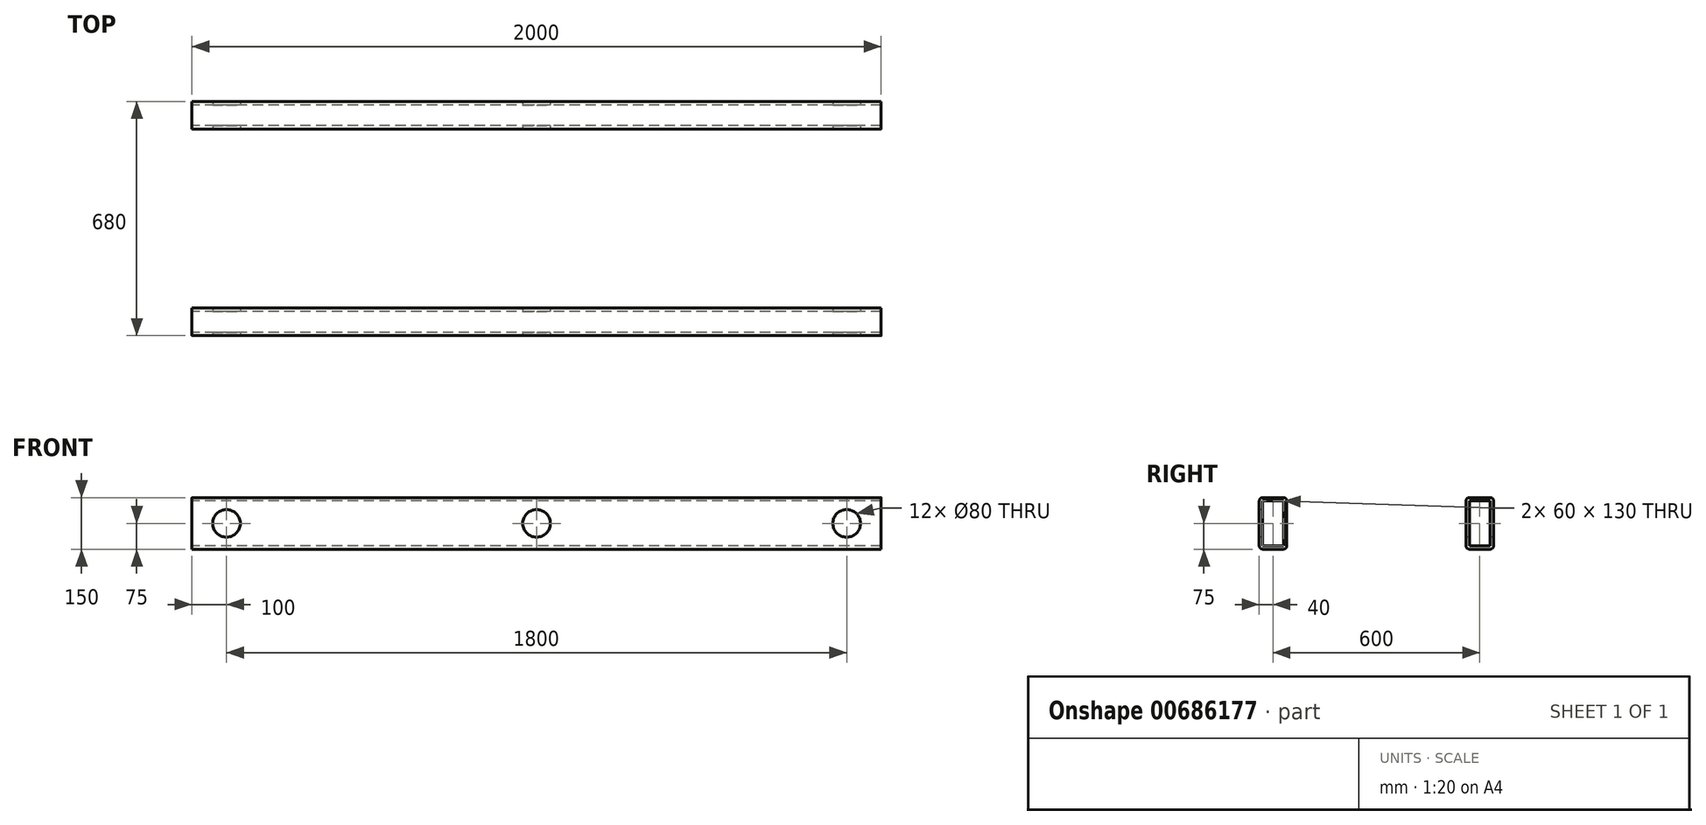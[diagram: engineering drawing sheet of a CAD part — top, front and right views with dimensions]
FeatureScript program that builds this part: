
annotation { "Feature Type Name" : "Feature", "Feature Type Description" : "" }
export const myFeature = defineFeature(function(context is Context, id is Id, definition is map)
    precondition{}
    {
        {
            var Q0;
            Q0=qCreatedBy(makeId("Right.planeOp"),FACE);
            var sketch = newSketch(context, id + "F0", { "sketchPlane" : qUnion([Q0])});
            skLineSegment(sketch, "E0.rect.bottom", {"start": v(-270, -75) * mm, "end": v(-330, -75) * mm});
            skLineSegment(sketch, "E0.rect.top", {"start": v(-270, 75) * mm, "end": v(-330, 75) * mm});
            skLineSegment(sketch, "E0.rect.left", {"start": v(-260, -65) * mm, "end": v(-260, 65) * mm});
            skLineSegment(sketch, "E0.rect.right", {"start": v(-340, -65) * mm, "end": v(-340, 65) * mm});
            skPoint(sketch, "E0.rect.middle", {"position": v(-300, 0) * mm});
            skPoint(sketch, "E1.visualSharp", {"position": v(-340, 75) * mm});
            skArc(sketch, "E1.filletArc", {"start": v(-330, 75) * mm, "mid": v(-337.07, 72.07) * mm, "end": v(-340, 65) * mm});
            skPoint(sketch, "E2.visualSharp", {"position": v(-260, 75) * mm});
            skArc(sketch, "E2.filletArc", {"start": v(-260, 65) * mm, "mid": v(-262.93, 72.07) * mm, "end": v(-270, 75) * mm});
            skPoint(sketch, "E3.visualSharp", {"position": v(-260, -75) * mm});
            skArc(sketch, "E3.filletArc", {"start": v(-270, -75) * mm, "mid": v(-262.93, -72.07) * mm, "end": v(-260, -65) * mm});
            skPoint(sketch, "E4.visualSharp", {"position": v(-340, -75) * mm});
            skArc(sketch, "E4.filletArc", {"start": v(-340, -65) * mm, "mid": v(-337.07, -72.07) * mm, "end": v(-330, -75) * mm});
            skLineSegment(sketch, "E5.0", {"start": v(-270, 65) * mm, "end": v(-330, 65) * mm});
            skLineSegment(sketch, "E5.1", {"start": v(-270, -65) * mm, "end": v(-270, 65) * mm});
            skLineSegment(sketch, "E5.2", {"start": v(-270, -65) * mm, "end": v(-330, -65) * mm});
            skLineSegment(sketch, "E5.3", {"start": v(-330, -65) * mm, "end": v(-330, 65) * mm});
            skArc(sketch, "E6.MirrorCS", {"start": v(330, 75) * mm, "mid": v(337.07, 72.07) * mm, "end": v(340, 65) * mm});
            skArc(sketch, "E7.MirrorCS", {"start": v(260, 65) * mm, "mid": v(262.93, 72.07) * mm, "end": v(270, 75) * mm});
            skArc(sketch, "E8.MirrorCS", {"start": v(340, -65) * mm, "mid": v(337.07, -72.07) * mm, "end": v(330, -75) * mm});
            skArc(sketch, "E9.MirrorCS", {"start": v(270, -75) * mm, "mid": v(262.93, -72.07) * mm, "end": v(260, -65) * mm});
            skLineSegment(sketch, "E10.MirrorCS", {"start": v(270, -75) * mm, "end": v(330, -75) * mm});
            skPoint(sketch, "E11.MirrorP", {"position": v(340, -75) * mm});
            skLineSegment(sketch, "E12.MirrorCS", {"start": v(330, -65) * mm, "end": v(330, 65) * mm});
            skPoint(sketch, "E13.MirrorP", {"position": v(260, 75) * mm});
            skPoint(sketch, "E14.MirrorP", {"position": v(340, 75) * mm});
            skLineSegment(sketch, "E15.MirrorCS", {"start": v(270, -65) * mm, "end": v(330, -65) * mm});
            skPoint(sketch, "E16.MirrorP", {"position": v(300, 0) * mm});
            skLineSegment(sketch, "E17.MirrorCS", {"start": v(270, -65) * mm, "end": v(270, 65) * mm});
            skLineSegment(sketch, "E18.MirrorCS", {"start": v(270, 75) * mm, "end": v(330, 75) * mm});
            skPoint(sketch, "E19.MirrorP", {"position": v(260, -75) * mm});
            skLineSegment(sketch, "E20.MirrorCS", {"start": v(260, -65) * mm, "end": v(260, 65) * mm});
            skLineSegment(sketch, "E21.MirrorCS", {"start": v(270, 65) * mm, "end": v(330, 65) * mm});
            skLineSegment(sketch, "E22.MirrorCS", {"start": v(340, -65) * mm, "end": v(340, 65) * mm});
            skSolve(sketch);
        }
        {
            var Q0;
            Q0=qSketchRegion(id+"F0",true);
            extrude(context, id + "F1", {"entities" : qUnion([Q0]), "endBound" : BoundingType.SYMMETRIC, "depth" : 2000 * mm});
        }
        {
            var Q0;
            Q0=qCreatedBy(makeId("Front.planeOp"),FACE);
            var sketch = newSketch(context, id + "F2", { "sketchPlane" : qUnion([Q0])});
            skCircle(sketch, "E23", {"center": v(900, 0) * mm, "radius": 50 * mm});
            skCircle(sketch, "E24", {"center": v(900, 0) * mm, "radius": 40 * mm});
            skCircle(sketch, "E25.1.0.0", {"center": v(0, 0) * mm, "radius": 50 * mm});
            skCircle(sketch, "E25.1.0.1", {"center": v(0, 0) * mm, "radius": 40 * mm});
            skCircle(sketch, "E25.2.0.0", {"center": v(-900, 0) * mm, "radius": 50 * mm});
            skCircle(sketch, "E25.2.0.1", {"center": v(-900, 0) * mm, "radius": 40 * mm});
            skLineSegment(sketch, "E25.direction1", {"start": v(900, 0) * mm, "end": v(0, 0) * mm, "construction": true});
            skSolve(sketch);
        }
        {
            var Q0;
            Q0=makeQuery(id+"F2.imprint","IMPRINT",FACE,{"disambiguationData":[TD([[makeQuery(id+"F2.imprint","IMPRINT",EDGE,{"derivedFrom":sQuery(id+"F2.wireOp",EDGE,"E24")}),1.0]])]});
            var Q1;
            Q1=makeQuery(id+"F2.imprint","IMPRINT",FACE,{"disambiguationData":[TD([[makeQuery(id+"F2.imprint","IMPRINT",EDGE,{"derivedFrom":sQuery(id+"F2.wireOp",EDGE,"E25.1.0.1")}),1.0]])]});
            var Q2;
            Q2=makeQuery(id+"F2.imprint","IMPRINT",FACE,{"disambiguationData":[TD([[makeQuery(id+"F2.imprint","IMPRINT",EDGE,{"derivedFrom":sQuery(id+"F2.wireOp",EDGE,"E25.2.0.1")}),1.0]])]});
            extrude(context, id + "F3", {"entities" : qUnion([Q0, Q1, Q2]), "operationType" : NewBodyOperationType.REMOVE, "endBound" : BoundingType.THROUGH_ALL, "oppositeDirection" : true, "depth" : 25 * mm, "hasSecondDirection" : true, "secondDirectionBound" : SecondDirectionBoundingType.THROUGH_ALL, "secondDirectionOppositeDirection" : false, "secondDirectionDepth" : 25 * mm});
        }
    });
